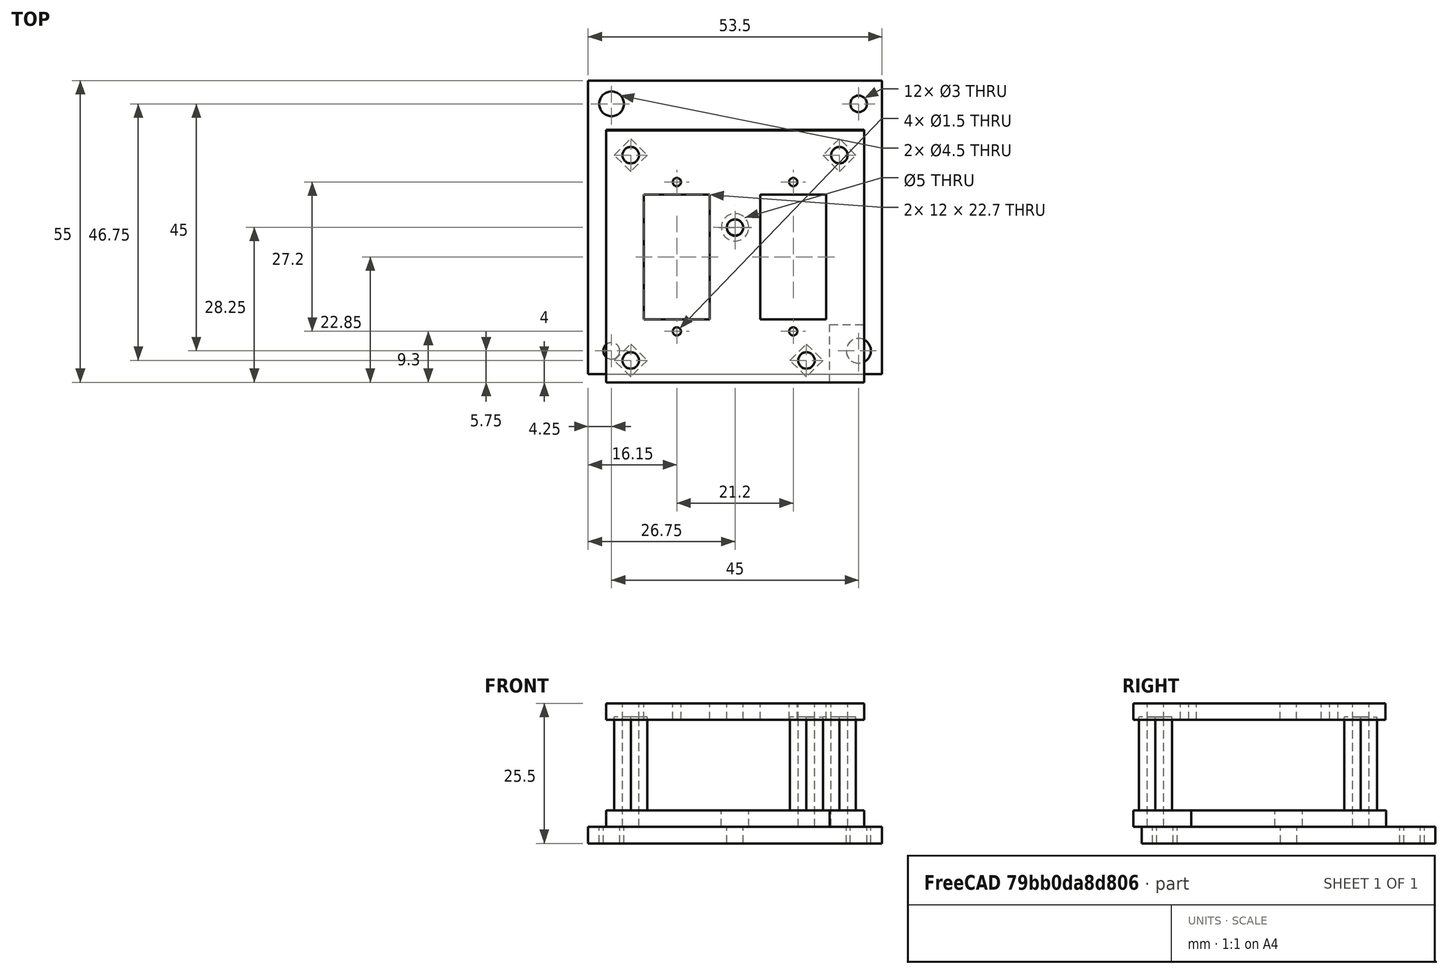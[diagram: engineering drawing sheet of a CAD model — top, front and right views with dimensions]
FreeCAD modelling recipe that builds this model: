
FCSTD DOCUMENT  (FreeCAD 0.17R13541 (Git))
Label: Fuel Temp Gauge
License: All rights reserved
LicenseURL: http://en.wikipedia.org/wiki/All_rights_reserved
objects: Part::Cylinder×12, Part::Cut×9, Part::FeaturePython×7, Part::Box×5, Part::Fuse×3, Part::Prism×3, Part::MultiFuse×3
note: 42 computed .brp shape members not serialized (recipe doc carries the construction recipe); baked Part::Feature solids carry a one-line shape summary decoded from their .brp

FEATURE [Part::Box] Box  label="Placa original"
  AttacherType = Attacher::AttachEngine3D
  Height = 3
  Length = 53.5
  Width = 53.5
FEATURE [Part::Cylinder] Cylinder  label="Taladro 1"
  Angle = 360
  AttacherType = Attacher::AttachEngine3D
  Height = 10
  Placement = pos=(4.25,49.25,-4) rot=(0,0,1;0rad)
  Radius = 2.25
FEATURE [Part::FeaturePython] Array  label="Array taladro 1"  # Draft array (typed FeaturePython)
  Angle = 360
  ArrayType = 0
  Axis = (0,0,1)
  Base = -> Cylinder
  Center = (0,0,0)
  Fuse = false
  IntervalAxis = (0,0,0)
  IntervalX = (45,-45,0)
  IntervalY = (0,1,0)
  IntervalZ = (0,0,0)
  NumberPolar = 1
  NumberX = 2
  NumberY = 1
  NumberZ = 1
FEATURE [Part::Cylinder] Cylinder001  label="Taladro 2"
  Angle = 360
  AttacherType = Attacher::AttachEngine3D
  Height = 10
  Placement = pos=(4.25,4.25,0) rot=(0,0,1;0rad)
  Radius = 1.5
FEATURE [Part::FeaturePython] Array001  label="Array taladro 2"  # Draft array (typed FeaturePython)
  Angle = 360
  ArrayType = 0
  Axis = (0,0,1)
  Base = -> Cylinder001
  Center = (0,0,0)
  Fuse = false
  IntervalAxis = (0,0,0)
  IntervalX = (22.5,22.5,0)
  IntervalY = (0,1,0)
  IntervalZ = (0,0,0)
  NumberPolar = 1
  NumberX = 3
  NumberY = 1
  NumberZ = 1
FEATURE [Part::Fuse] Fusion  label="Taladros"
  Base = -> Array
  Refine = true
  Tool = -> Array001
FEATURE [Part::Cut] Cut  label="Fuel Temp Plate"
  Base = -> Box
  Refine = true
  Tool = -> Fusion
FEATURE [Part::Box] Box001  label="top plate 2"
  AttacherType = Attacher::AttachEngine3D
  Height = 3
  Length = 47
  Placement = pos=(3.25,-1.5,3) rot=(0,0,1;0rad)
  Width = 46
FEATURE [Part::Cylinder] Cylinder002  label="taladro 3"
  Angle = 360
  AttacherType = Attacher::AttachEngine3D
  Height = 10
  Placement = pos=(26.75,26.75,0) rot=(0,0,1;0rad)
  Radius = 2.5
FEATURE [Part::Cylinder] Cylinder003  label="taladro 4"
  Angle = 360
  AttacherType = Attacher::AttachEngine3D
  Height = 27
  Placement = pos=(7.75,2.5,0) rot=(0,0,1;0rad)
  Radius = 1.5
FEATURE [Part::FeaturePython] Array002  label="Array taladro 4"  # Draft array (typed FeaturePython)
  Angle = 360
  ArrayType = 0
  Axis = (0,0,1)
  Base = -> Cylinder003
  Center = (0,0,0)
  Fuse = false
  IntervalAxis = (0,0,0)
  IntervalX = (38,0,0)
  IntervalY = (0,37.4,0)
  IntervalZ = (0,0,0)
  NumberPolar = 1
  NumberX = 1
  NumberY = 2
  NumberZ = 1
FEATURE [Part::Prism] Prism  label="Columna"
  AttacherType = Attacher::AttachEngine3D
  Circumradius = 3
  Height = 20
  Placement = pos=(7.75,2.5,3) rot=(0,0,1;0rad)
  Polygon = 4
FEATURE [Part::FeaturePython] Array003  label="Array columnas"  # Draft array (typed FeaturePython)
  Angle = 360
  ArrayType = 0
  Axis = (0,0,1)
  Base = -> Prism
  Center = (0,0,0)
  Fuse = false
  IntervalAxis = (0,0,0)
  IntervalX = (38,0,0)
  IntervalY = (0,37.4,0)
  IntervalZ = (0,0,0)
  NumberPolar = 1
  NumberX = 1
  NumberY = 2
  NumberZ = 1
FEATURE [Part::Fuse] Fusion001  label="top plate columnas"
  Base = -> Box001
  Refine = true
  Tool = -> Array003
FEATURE [Part::Fuse] Fusion002  label="Taladros 2"
  Base = -> Cylinder002
  Refine = true
  Tool = -> Array002
FEATURE [Part::Cut] Cut001  label="Top plate"
  Base = -> Fusion001
  Refine = true
  Tool = -> Fusion002
FEATURE [Part::Box] Box002  label="base 2"
  AttacherType = Attacher::AttachEngine3D
  Height = 3
  Length = 47
  Placement = pos=(3.25,-1.5,22.5) rot=(0,0,1;0rad)
  Width = 45.9
FEATURE [Part::Box] Box003  label="Taladro servomotor"
  AttacherType = Attacher::AttachEngine3D
  Height = 10
  Length = 12
  Placement = pos=(10.15,10,19.5) rot=(0,0,1;0rad)
  Width = 22.7
FEATURE [Part::FeaturePython] Array004  label="Array taladro servomotor"  # Draft array (typed FeaturePython)
  Angle = 360
  ArrayType = 0
  Axis = (0,0,1)
  Base = -> Box003
  Center = (0,0,0)
  Fuse = false
  IntervalAxis = (0,0,0)
  IntervalX = (21.2,0,0)
  IntervalY = (0,1,0)
  IntervalZ = (0,0,0)
  NumberPolar = 1
  NumberX = 2
  NumberY = 1
  NumberZ = 1
FEATURE [Part::Cylinder] Cylinder004  label="taladro 5"
  Angle = 360
  AttacherType = Attacher::AttachEngine3D
  Height = 10
  Placement = pos=(7.75,2.5,19.5) rot=(0,0,1;0rad)
  Radius = 1.5
FEATURE [Part::FeaturePython] Array005  label="Array taladro 5"  # Draft array (typed FeaturePython)
  Angle = 360
  ArrayType = 0
  Axis = (0,0,1)
  Base = -> Cylinder004
  Center = (0,0,0)
  Fuse = false
  IntervalAxis = (0,0,0)
  IntervalX = (38,0,0)
  IntervalY = (0,37.4,0)
  IntervalZ = (0,0,0)
  NumberPolar = 1
  NumberX = 1
  NumberY = 2
  NumberZ = 1
FEATURE [Part::Cylinder] Cylinder005  label="Taladro 6"
  Angle = 360
  AttacherType = Attacher::AttachEngine3D
  Height = 10
  Placement = pos=(26.75,26.7,19.5) rot=(0,0,1;0rad)
  Radius = 1.5
FEATURE [Part::Cylinder] Cylinder006  label="Taladro 7"
  Angle = 360
  AttacherType = Attacher::AttachEngine3D
  Height = 10
  Placement = pos=(16.15,7.8,19.5) rot=(0,0,1;0rad)
  Radius = 0.75
FEATURE [Part::FeaturePython] Array006  label="Array taladros 7"  # Draft array (typed FeaturePython)
  Angle = 360
  ArrayType = 0
  Axis = (0,0,1)
  Base = -> Cylinder006
  Center = (0,0,0)
  Fuse = false
  IntervalAxis = (0,0,0)
  IntervalX = (21.2,0,0)
  IntervalY = (0,27.2,0)
  IntervalZ = (0,0,0)
  NumberPolar = 1
  NumberX = 2
  NumberY = 2
  NumberZ = 1
FEATURE [Part::MultiFuse] Fusion003  label="Taladros 3"
  Refine = true
  Shapes = -> [Cylinder005,Array006,Array004,Array005]
FEATURE [Part::Cut] Cut002  label="base previa"
  Base = -> Box002
  Refine = true
  Tool = -> Fusion003
FEATURE [Part::Prism] Prism001  label="Columna 3"
  AttacherType = Attacher::AttachEngine3D
  Circumradius = 3
  Height = 20
  Placement = pos=(45.75,39.9,3) rot=(0,0,1;0rad)
  Polygon = 4
FEATURE [Part::Cylinder] Cylinder007  label="taladro adicional 3"
  Angle = 360
  AttacherType = Attacher::AttachEngine3D
  Height = 27
  Placement = pos=(45.75,39.9,0) rot=(0,0,1;0rad)
  Radius = 1.5
FEATURE [Part::MultiFuse] Fusion004  label="placa con tres taladros"
  Refine = true
  Shapes = -> [Cut001,Prism001]
FEATURE [Part::Cut] Cut003  label="Placa con tres columnas"
  Base = -> Fusion004
  Refine = true
  Tool = -> Cylinder007
FEATURE [Part::Box] Box004  label="Recorte placa"
  AttacherType = Attacher::AttachEngine3D
  Height = 3
  Length = 10
  Placement = pos=(44,-2,3) rot=(0,0,1;0rad)
  Width = 11
FEATURE [Part::Cut] Cut004  label="Placa tres columnas y tornillo"
  Base = -> Cut003
  Refine = true
  Tool = -> Box004
FEATURE [Part::Prism] Prism002  label="Columna 4"
  AttacherType = Attacher::AttachEngine3D
  Circumradius = 3
  Height = 20
  Placement = pos=(39.75,2.5,3) rot=(0,0,1;0rad)
  Polygon = 4
FEATURE [Part::Cylinder] Cylinder008  label="taladro adicional 4"
  Angle = 360
  AttacherType = Attacher::AttachEngine3D
  Height = 27
  Placement = pos=(39.75,2.5,0) rot=(0,0,1;0rad)
  Radius = 1.5
FEATURE [Part::Cut] Cut005
  Base = -> Cut004
  Refine = true
  Tool = -> Cylinder008
FEATURE [Part::Cylinder] Cylinder009  label="taladro adicional 005"
  Angle = 360
  AttacherType = Attacher::AttachEngine3D
  Height = 27
  Placement = pos=(39.75,2.5,0) rot=(0,0,1;0rad)
  Radius = 1.5
FEATURE [Part::Cut] Cut006
  Base = -> Prism002
  Refine = true
  Tool = -> Cylinder009
FEATURE [Part::MultiFuse] Fusion005  label="top plate final"
  Refine = true
  Shapes = -> [Cut005,Cut006]
FEATURE [Part::Cylinder] Cylinder010  label="taladro 006"
  Angle = 360
  AttacherType = Attacher::AttachEngine3D
  Height = 10
  Placement = pos=(45.75,39.9,19.5) rot=(0,0,1;0rad)
  Radius = 1.5
FEATURE [Part::Cylinder] Cylinder011  label="taladro 007"
  Angle = 360
  AttacherType = Attacher::AttachEngine3D
  Height = 10
  Placement = pos=(39.75,2.5,18.5) rot=(0,0,1;0rad)
  Radius = 1.5
FEATURE [Part::Cut] Cut007  label="base 3 taladros"
  Base = -> Cut002
  Refine = true
  Tool = -> Cylinder010
FEATURE [Part::Cut] Cut008  label="base final"
  Base = -> Cut007
  Refine = true
  Tool = -> Cylinder011
